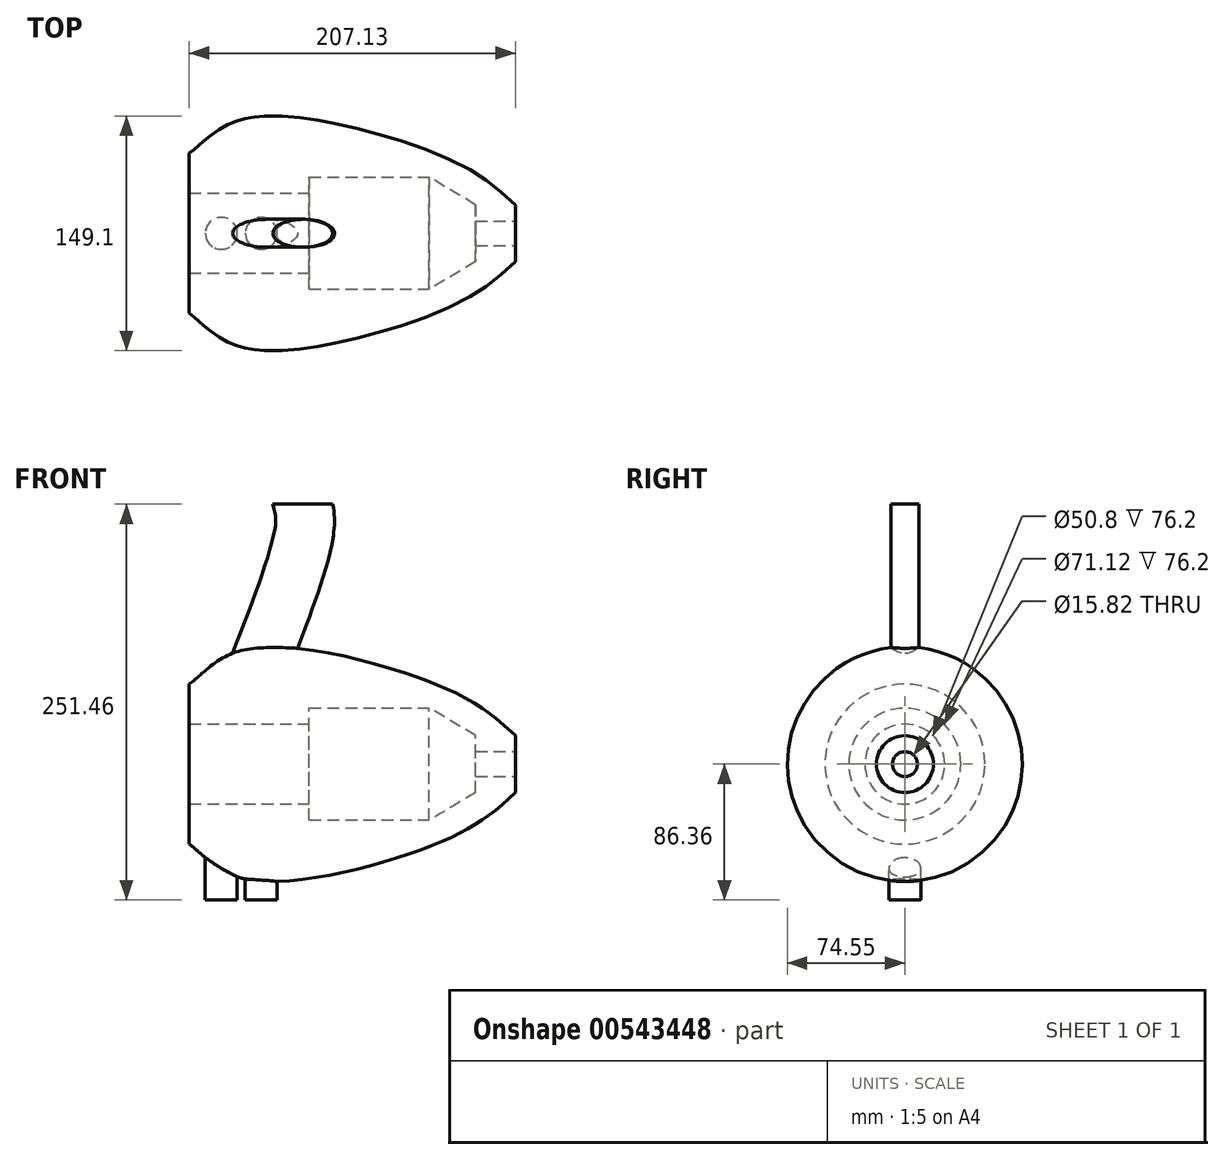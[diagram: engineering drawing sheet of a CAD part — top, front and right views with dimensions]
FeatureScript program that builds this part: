
annotation { "Feature Type Name" : "Feature", "Feature Type Description" : "" }
export const myFeature = defineFeature(function(context is Context, id is Id, definition is map)
    precondition{}
    {
        {
            var Q0;
            Q0=qCreatedBy(makeId("Front.planeOp"),FACE);
            var sketch = newSketch(context, id + "F0", { "sketchPlane" : qUnion([Q0])});
            skLineSegment(sketch, "E0", {"start": v(207.13, -32.73) * mm, "end": v(207.13, -42.9) * mm});
            skLineSegment(sketch, "E1", {"start": v(207.13, -42.9) * mm, "end": v(181.83, -42.9) * mm});
            skLineSegment(sketch, "E2", {"start": v(181.83, -42.9) * mm, "end": v(181.83, -32.73) * mm});
            skLineSegment(sketch, "E3", {"start": v(181.83, -32.73) * mm, "end": v(152.4, -15.24) * mm});
            skLineSegment(sketch, "E4", {"start": v(152.4, -15.24) * mm, "end": v(76.2, -15.24) * mm});
            skLineSegment(sketch, "E5", {"start": v(76.2, -15.24) * mm, "end": v(76.2, -25.4) * mm});
            skLineSegment(sketch, "E6", {"start": v(76.2, -25.4) * mm, "end": v(0, -25.4) * mm});
            skLineSegment(sketch, "E7", {"start": v(0, -25.4) * mm, "end": v(0, 0) * mm});
            skLineSegment(sketch, "E8", {"start": v(235.98, -50.8) * mm, "end": v(-92.51, -50.8) * mm, "construction": true});
            skFitSpline(sketch, "E9", {"points": [v(0, 0) * mm, v(36.88, 22.47) * mm, v(156.33, 0) * mm, v(207.13, -32.73) * mm], "startDerivative": vector(121.2, 94.14) * mm, "endDerivative": vector(156.12, -146.25) * mm});
            skSolve(sketch);
        }
        {
            var Q0;
            Q0=qSketchRegion(id+"F0",true);
            var Q1;
            Q1=makeQuery(id+"F0.imprint","IMPRINT",FACE,{"disambiguationData":[TD([[makeQuery(id+"F0.imprint","IMPRINT",EDGE,{"derivedFrom":sQuery(id+"F0.wireOp",EDGE,"8QcmkIuE-P2bz-makn-afnb-PRppPDIcpb41")}),-1.0]])]});
            var Q2;
            Q2=sQuery(id+"F0.wireOp",EDGE,"E8");
            revolve(context, id + "F1", {"entities" : qUnion([Q0, Q1]), "axis" : qUnion([Q2]), "revolveType" : RevolveType.FULL});
        }
        {
            var Q0;
            Q0=qCreatedBy(makeId("Top.planeOp"),FACE);
            cPlane(context, id + "F2", {"entities" : qUnion([Q0]), "cplaneType" : CPlaneType.OFFSET, "offset" : 101.6 * mm, "oppositeDirection" : true, "width" : 152.4 * mm, "height" : 152.4 * mm});
        }
        {
            var Q0;
            Q0=qCreatedBy(id+"F2.planeOp",FACE);
            var sketch = newSketch(context, id + "F3", { "sketchPlane" : qUnion([Q0])});
            skLineSegment(sketch, "E10", {"start": v(0, 0) * mm, "end": v(20.32, 0) * mm, "construction": true});
            skLineSegment(sketch, "E11", {"start": v(20.32, 0) * mm, "end": v(45.72, 0) * mm, "construction": true});
            skCircle(sketch, "E12", {"center": v(20.32, 0) * mm, "radius": 10.16 * mm});
            skCircle(sketch, "E13", {"center": v(45.72, 0) * mm, "radius": 10.16 * mm});
            skSolve(sketch);
        }
        {
            var Q0;
            Q0=makeQuery(id+"F3.imprint","IMPRINT",FACE,{"disambiguationData":[TD([[makeQuery(id+"F3.imprint","IMPRINT",EDGE,{"derivedFrom":sQuery(id+"F3.wireOp",EDGE,"E12")}),1.0]])]});
            var Q1;
            Q1=makeQuery(id+"F3.imprint","IMPRINT",FACE,{"disambiguationData":[TD([[makeQuery(id+"F3.imprint","IMPRINT",EDGE,{"derivedFrom":sQuery(id+"F3.wireOp",EDGE,"E13")}),1.0]])]});
            extrude(context, id + "F4", {"entities" : qUnion([Q0, Q1]), "operationType" : NewBodyOperationType.ADD, "oppositeDirection" : true, "depth" : 35.56 * mm, "offsetDistance" : 25.4 * mm});
        }
        {
            var Q0;
            Q0=qCreatedBy(makeId("Front.planeOp"),FACE);
            var sketch = newSketch(context, id + "F5", { "sketchPlane" : qUnion([Q0])});
            skFitSpline(sketch, "E14", {"points": [v(39.89, 0) * mm, v(72.8, 96.37) * mm, v(72.07, 114.3) * mm], "startDerivative": vector(64.02, 163.65) * mm, "endDerivative": vector(-9.69, 49.38) * mm});
            skSolve(sketch);
        }
        {
            var Q0;
            Q0=qCreatedBy(makeId("Top.planeOp"),FACE);
            cPlane(context, id + "F6", {"entities" : qUnion([Q0]), "cplaneType" : CPlaneType.OFFSET, "offset" : 114.3 * mm, "width" : 152.4 * mm, "height" : 152.4 * mm});
        }
        {
            var Q0;
            Q0=qCreatedBy(id+"F6.planeOp",FACE);
            var sketch = newSketch(context, id + "F7", { "sketchPlane" : qUnion([Q0])});
            skEllipse(sketch, "E15", {"center": v(72.07, 0) * mm, "majorRadius": 19.05 * mm, "minorRadius": 8.9 * mm, "majorAxis": v(-1, 0)});
            skSolve(sketch);
        }
        {
            var Q0;
            Q0=makeQuery(id+"F7.imprint","IMPRINT",FACE,{"disambiguationData":[TD([[makeQuery(id+"F7.imprint","IMPRINT",EDGE,{"derivedFrom":sQuery(id+"F7.wireOp",EDGE,"E15")}),1.0]])]});
            var Q1;
            Q1=sQuery(id+"F5.wireOp",EDGE,"E14");
            sweep(context, id + "F8", {"operationType" : NewBodyOperationType.ADD, "profiles" : qUnion([Q0]), "path" : qUnion([Q1])});
        }
    });
